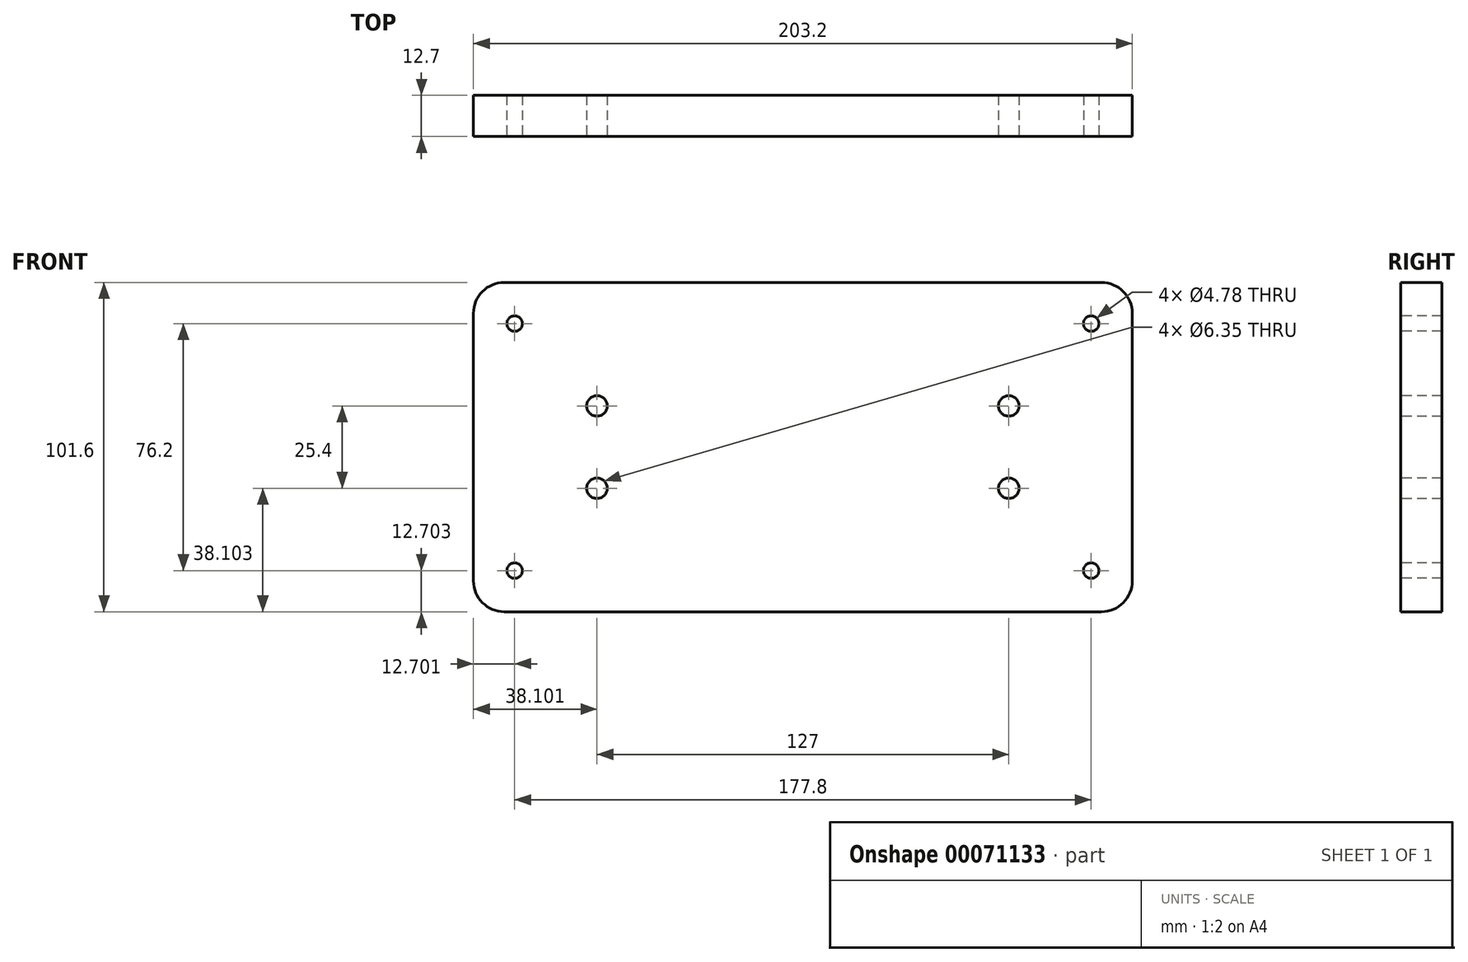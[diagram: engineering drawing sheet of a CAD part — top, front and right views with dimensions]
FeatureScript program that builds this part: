
annotation { "Feature Type Name" : "Feature", "Feature Type Description" : "" }
export const myFeature = defineFeature(function(context is Context, id is Id, definition is map)
    precondition{}
    {
        {
            var Q0;
            Q0=qCreatedBy(makeId("Front.planeOp"),FACE);
            var sketch = newSketch(context, id + "F0", { "sketchPlane" : qUnion([Q0])});
            skLineSegment(sketch, "E0.bottom", {"start": v(-100.22, 59.07) * mm, "end": v(102.98, 59.07) * mm});
            skLineSegment(sketch, "E0.top", {"start": v(-100.22, -42.53) * mm, "end": v(102.98, -42.53) * mm});
            skLineSegment(sketch, "E0.left", {"start": v(-100.22, 59.07) * mm, "end": v(-100.22, -42.53) * mm});
            skLineSegment(sketch, "E0.right", {"start": v(102.98, 59.07) * mm, "end": v(102.98, -42.53) * mm});
            skSolve(sketch);
        }
        {
            var Q0;
            Q0=makeQuery(id+"F0.imprint","IMPRINT",FACE,{"disambiguationData":[TD([[makeQuery(id+"F0.imprint","IMPRINT",EDGE,{"derivedFrom":sQuery(id+"F0.wireOp",EDGE,"E0.bottom")}),-1.0]])]});
            extrude(context, id + "F1", {"entities" : qUnion([Q0]), "depth" : 12.7 * mm});
        }
        {
            var Q0;
            Q0=makeQuery(id+"F1.opExtrude","SWEPT_EDGE",EDGE,{"disambiguationData":[OSD([sQuery(id+"F0.wireOp",EDGE,"E0.bottom"),sQuery(id+"F0.wireOp",EDGE,"E0.left")])]});
            var Q1;
            Q1=makeQuery(id+"F1.opExtrude","SWEPT_EDGE",EDGE,{"disambiguationData":[OSD([sQuery(id+"F0.wireOp",EDGE,"E0.bottom"),sQuery(id+"F0.wireOp",EDGE,"E0.right")])]});
            var Q2;
            Q2=makeQuery(id+"F1.opExtrude","SWEPT_EDGE",EDGE,{"disambiguationData":[OSD([sQuery(id+"F0.wireOp",EDGE,"E0.top"),sQuery(id+"F0.wireOp",EDGE,"E0.right")])]});
            var Q3;
            Q3=makeQuery(id+"F1.opExtrude","SWEPT_EDGE",EDGE,{"disambiguationData":[OSD([sQuery(id+"F0.wireOp",EDGE,"E0.top"),sQuery(id+"F0.wireOp",EDGE,"E0.left")])]});
            fillet(context, id + "F2", {"entities" : qUnion([Q0, Q1, Q2, Q3]), "radius" : 9.52 * mm, "tangentPropagation" : true, "allowEdgeOverflow" : false});
        }
        {
            var Q0;
            Q0=makeQuery(id+"F1.opExtrude","CAP_FACE",FACE,{"disambiguationData":[OSD([sQuery(id+"F0.wireOp",EDGE,"E0.bottom"),sQuery(id+"F0.wireOp",EDGE,"E0.top"),sQuery(id+"F0.wireOp",EDGE,"E0.left"),sQuery(id+"F0.wireOp",EDGE,"E0.right")])],"isStart":false});
            var sketch = newSketch(context, id + "F3", { "sketchPlane" : qUnion([Q0])});
            skPoint(sketch, "E1", {"position": v(-87.52, 46.37) * mm});
            skPoint(sketch, "E2", {"position": v(90.28, 46.37) * mm});
            skPoint(sketch, "E3", {"position": v(-87.52, -29.83) * mm});
            skPoint(sketch, "E4", {"position": v(90.28, -29.83) * mm});
            skSolve(sketch);
        }
        {
            var Q0;
            Q0=sQuery(id+"F3.wireOp",VERTEX,"E1");
            var Q1;
            Q1=sQuery(id+"F3.wireOp",VERTEX,"E3");
            var Q2;
            Q2=sQuery(id+"F3.wireOp",VERTEX,"E2");
            var Q3;
            Q3=sQuery(id+"F3.wireOp",VERTEX,"E4");
            var Q4;
            Q4=makeQuery(id+"F1.opExtrude","SWEPT_BODY",BODY,{"disambiguationData":[OSD([sQuery(id+"F0.wireOp",EDGE,"E0.bottom"),sQuery(id+"F0.wireOp",EDGE,"E0.top"),sQuery(id+"F0.wireOp",EDGE,"E0.left"),sQuery(id+"F0.wireOp",EDGE,"E0.right")])]});
            hole(context, id + "F4", {"style" : HoleStyle.SIMPLE, "holeDiameter" : 4.78 * mm, "endStyle" : HoleEndStyle.THROUGH, "locations" : qUnion([Q0, Q1, Q2, Q3]), "scope" : qUnion([Q4])});
        }
        {
            var Q0;
            Q0=makeQuery(id+"F1.opExtrude","CAP_FACE",FACE,{"disambiguationData":[OSD([sQuery(id+"F0.wireOp",EDGE,"E0.bottom"),sQuery(id+"F0.wireOp",EDGE,"E0.top"),sQuery(id+"F0.wireOp",EDGE,"E0.left"),sQuery(id+"F0.wireOp",EDGE,"E0.right")])],"isStart":false});
            var sketch = newSketch(context, id + "F5", { "sketchPlane" : qUnion([Q0])});
            skPoint(sketch, "E5", {"position": v(-62.12, 20.97) * mm});
            skPoint(sketch, "E6", {"position": v(64.88, 20.97) * mm});
            skPoint(sketch, "E7", {"position": v(-62.12, -4.43) * mm});
            skPoint(sketch, "E8", {"position": v(64.88, -4.43) * mm});
            skSolve(sketch);
        }
        {
            var Q0;
            Q0=sQuery(id+"F5.wireOp",VERTEX,"E5");
            var Q1;
            Q1=sQuery(id+"F5.wireOp",VERTEX,"E7");
            var Q2;
            Q2=sQuery(id+"F5.wireOp",VERTEX,"E8");
            var Q3;
            Q3=sQuery(id+"F5.wireOp",VERTEX,"E6");
            var Q4;
            Q4=makeQuery(id+"F1.opExtrude","SWEPT_BODY",BODY,{"disambiguationData":[OSD([sQuery(id+"F0.wireOp",EDGE,"E0.bottom"),sQuery(id+"F0.wireOp",EDGE,"E0.top"),sQuery(id+"F0.wireOp",EDGE,"E0.left"),sQuery(id+"F0.wireOp",EDGE,"E0.right")])]});
            hole(context, id + "F6", {"style" : HoleStyle.SIMPLE, "holeDiameter" : 6.35 * mm, "endStyle" : HoleEndStyle.THROUGH, "locations" : qUnion([Q0, Q1, Q2, Q3]), "scope" : qUnion([Q4])});
        }
    });
